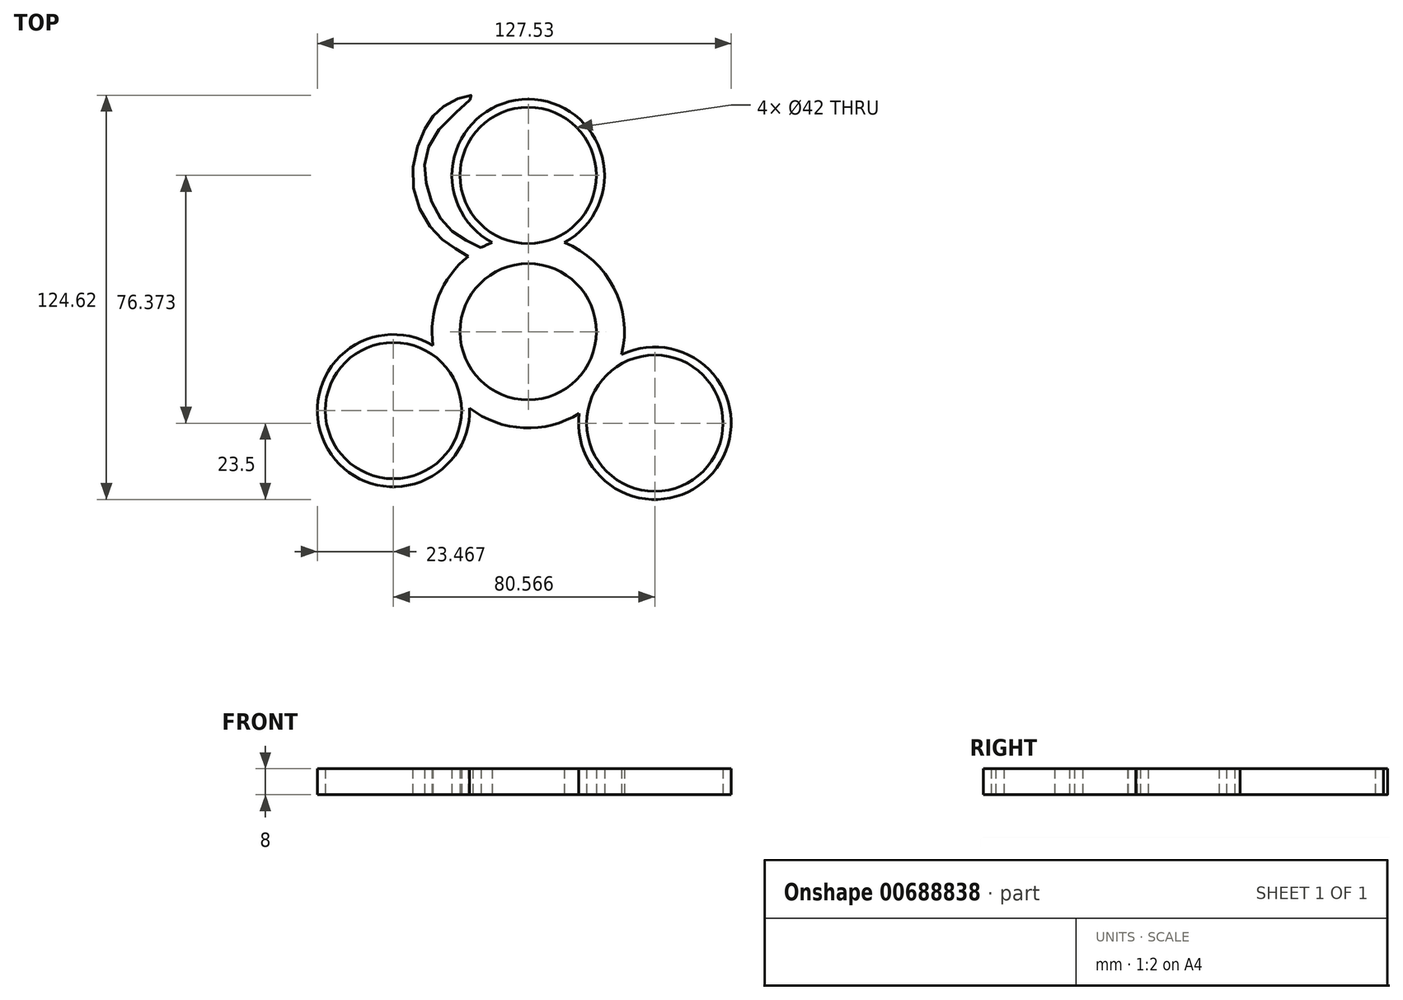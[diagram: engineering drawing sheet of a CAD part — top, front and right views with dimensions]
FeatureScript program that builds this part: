
annotation { "Feature Type Name" : "Feature", "Feature Type Description" : "" }
export const myFeature = defineFeature(function(context is Context, id is Id, definition is map)
    precondition{}
    {
        {
            var Q0;
            Q0=qCreatedBy(makeId("Top.planeOp"),FACE);
            var sketch = newSketch(context, id + "F0", { "sketchPlane" : qUnion([Q0])});
            skCircle(sketch, "E0", {"center": v(0, 0) * mm, "radius": 21 * mm});
            skCircle(sketch, "E1", {"center": v(0, 0) * mm, "radius": 24.66 * mm});
            skCircle(sketch, "E2", {"center": v(0, 0) * mm, "radius": 29.66 * mm});
            skPoint(sketch, "E3", {"position": v(21, 0) * mm});
            skPoint(sketch, "E4", {"position": v(0, 27.16) * mm});
            skCircle(sketch, "E5", {"center": v(0, 48.16) * mm, "radius": 21 * mm});
            skCircle(sketch, "E6", {"center": v(0, 48.16) * mm, "radius": 23.5 * mm});
            skPoint(sketch, "E7", {"position": v(21.88, -16.1) * mm});
            skCircle(sketch, "E8", {"center": v(39.03, -28.21) * mm, "radius": 21 * mm});
            skCircle(sketch, "E9", {"center": v(39.03, -28.21) * mm, "radius": 23.5 * mm});
            skPoint(sketch, "E10", {"position": v(-22.97, -14.5) * mm});
            skCircle(sketch, "E11", {"center": v(-41.53, -24.31) * mm, "radius": 21 * mm});
            skCircle(sketch, "E12", {"center": v(-41.53, -24.31) * mm, "radius": 23.46 * mm});
            skFitSpline(sketch, "E13", {"points": [v(-14.56, 25.84) * mm, v(-25.21, 32.65) * mm, v(-31.7, 47.15) * mm, v(-27.38, 62.43) * mm, v(-17.14, 72.74) * mm, v(-24.42, 70.5) * mm, v(-31.15, 63.78) * mm, v(-35.63, 46.4) * mm, v(-27.76, 29.57) * mm, v(-18.44, 23.24) * mm], "startDerivative": vector(-104.98, 53.84) * mm, "endDerivative": vector(89.03, -60.22) * mm});
            skPoint(sketch, "E14", {"position": v(-20.74, 68.95) * mm});
            skSolve(sketch);
        }
        {
            var Q0;
            Q0 = qSketchRegion(id + "F0", true);
            var Q1;
            Q1=makeQuery(id+"F0.imprint","IMPRINT",FACE,{"disambiguationData":[TD([[makeQuery(id+"F0.imprint","IMPRINT",EDGE,{"derivedFrom":sQuery(id+"F0.wireOp",EDGE,"E0")}),-1.0]])]});
            extrude(context, id + "F1", {"entities" : qUnion([Q0, Q1]), "depth" : 8 * mm, "offsetDistance" : 25 * mm});
        }
    });
